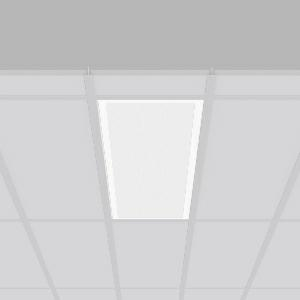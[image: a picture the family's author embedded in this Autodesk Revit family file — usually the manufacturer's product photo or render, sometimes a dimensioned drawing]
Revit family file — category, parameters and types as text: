
# Revit family: sidelite_eco_672374_002_1_07_9c77
name_source: partatom
category: Lighting Fixtures
units: mm (PartAtom-declared; Revit-internal decimal feet)

## family parameters
Cut with Voids When Loaded = No
Host = Face
Light Source = No
Part Type = Normal
Room Calculation Point = No
Round Connector Dimension = Use Diameter
Shared = No

## types (1)
- SIDELITE ECO (1 x LED Modul 840, 3500 lm, 4000)
    Apparent Load = 29 VA
    CIE Flux Codes = 59 87 97 100 100
    Color Rendering = 80
    Color Temperature = 4000
    Default Elevation = 1800 mm
    Description = Series: SIDELITE ECO
Highly economical recessed luminaire with progressive LED technology. For escape route illumination. Frame made of aluminium, powder-coated. Diffuser plastic microprismatic. Lightguide and diffuser made of non-yellowing plastic (PMMA). Lateral light emission (RZB SIDELITE technology) for homogeneous light distribution. External driver. Self-contained system with automatic self-test and feedback via DALI bus, only to RZB DALI monitoring system. External driver with simple plug-in locking system. Extended connection cable (1.90 m). 
Colour: white
Length: 1245 mm
Width: 308 mm
Cut-out length: 1220 mm
Cut-out width: 285 mm
Recess height: 160 mm
Luminaire: recess height: 40 mm
Weight: 4.7 kg
Operating mode: maintained power mode
Duration time: 3 h
Lamp: LED
Socket: without socket
Colour temperature: 4000K
Colour rendering index (CRI): 80
System power: 29 W
Rated luminous flux: 3500 lm
Luminous flux, emergency: 510 lm
System power, emergency: -
Control gear: Regulated power supply
Protection class: I
Type of protection: IP 20
    Height = 0 mm  [stored 0 ft]
    Lamp = 1 x LED Modul 840
    Lamp Light Flux = 3500 lm
    Lamp count = 1
    Length = 1245 mm
    Lifetime = 50000 h
    Luminous efficacy = 121 lm/W
    Manufacturer = RZB
    ModVariant = No
    Model = 672374.002.1.07
    Mounting Place = Ceiling
    Mounting Type = Recessed
    Number of Poles = 1
    OnlyDefault = Yes
    Power Factor = 1
    Product Name = SIDELITE ECO
    Product group = Recessed modular luminaires
    ProductGroupID = 406
    Protection Class = Protection class I
    Protection Degree = IP 20
    RLX_Detail_Level = 1
    RLX_Emergency_Light_Flux = 510 lm
    RLX_Emergency_Type = 3
    RLX_Emergency_Type_DB = Yes
    RlxData = <blob elided: 34353 chars, md5=b04630ba>
    Socket = socket
    Standby Power = 0 W
    System Light Flux = 3500 lm
    System Power = 29 W
    Type Comments = Product without accessories
    Type Image = 312368.002.jpg
    URL = http://relux.com
    VarID = ---
    Voltage = 230 V
    Voltage Range = 220-240 V
    Weight = 0.00 kg
    Width = 308 mm

note: [stored X ft] marks values corroborated as IEEE doubles in the binary element streams (Revit-internal decimal feet)

## geometry (parser evidence)
native form markers: Blend x4, Sweep x12
no freeform markers — native parametric forms only
